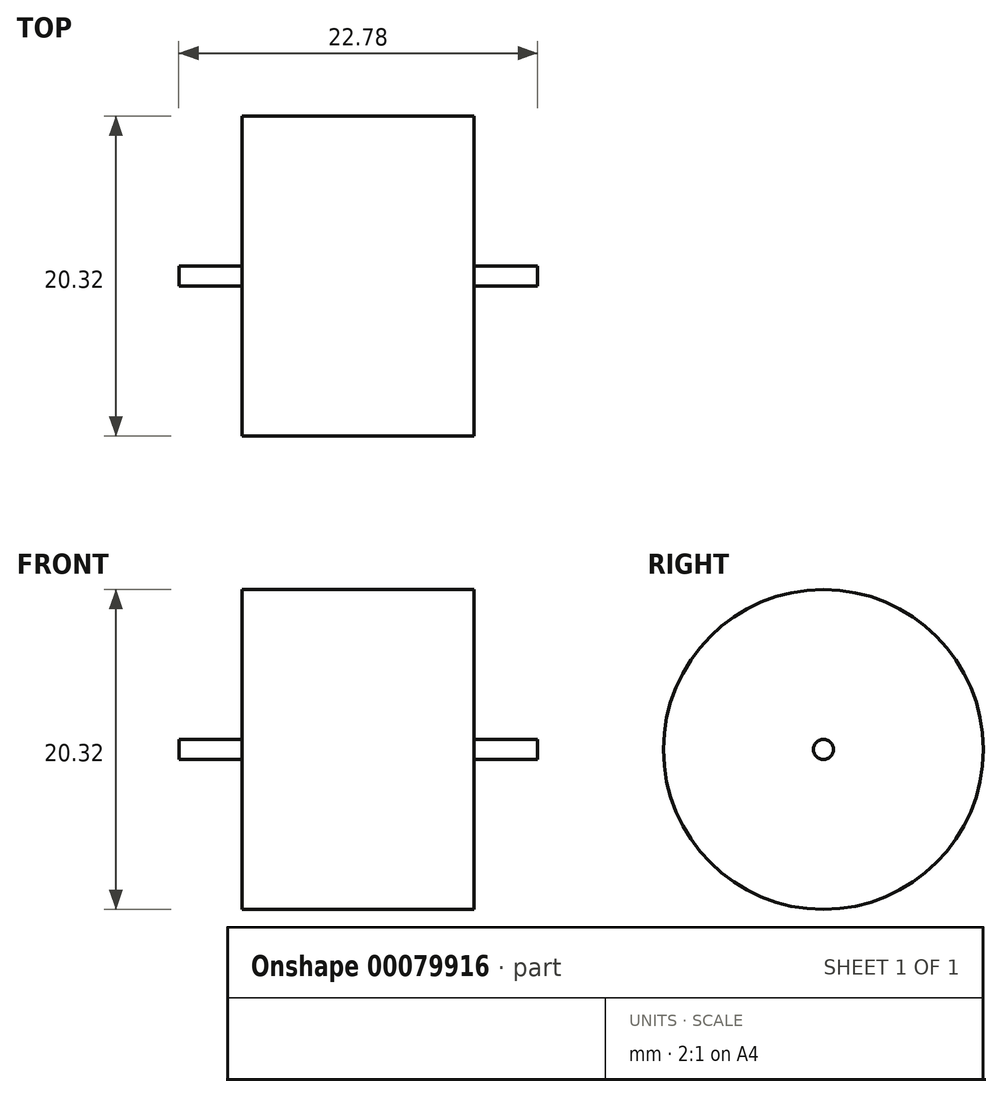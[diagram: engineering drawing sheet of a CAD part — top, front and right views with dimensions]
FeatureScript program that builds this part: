
annotation { "Feature Type Name" : "Feature", "Feature Type Description" : "" }
export const myFeature = defineFeature(function(context is Context, id is Id, definition is map)
    precondition{}
    {
        {
            var Q0;
            Q0=qCreatedBy(makeId("Right.planeOp"),FACE);
            var sketch = newSketch(context, id + "F0", { "sketchPlane" : qUnion([Q0])});
            skCircle(sketch, "E0", {"center": v(0, 0) * mm, "radius": 10.16 * mm});
            skCircle(sketch, "E1", {"center": v(0, 0) * mm, "radius": 0.64 * mm});
            skSolve(sketch);
        }
        {
            var Q0;
            Q0=makeQuery(id+"F0.imprint","IMPRINT",FACE,{"disambiguationData":[TD([[makeQuery(id+"F0.imprint","IMPRINT",EDGE,{"derivedFrom":sQuery(id+"F0.wireOp",EDGE,"E0")}),1.0]])]});
            extrude(context, id + "F1", {"entities" : qUnion([Q0]), "depth" : 7.37 * mm, "hasSecondDirection" : true, "secondDirectionOppositeDirection" : true, "secondDirectionDepth" : 7.37 * mm});
        }
        {
            var Q0;
            Q0=makeQuery(id+"F0.imprint","IMPRINT",FACE,{"disambiguationData":[TD([[makeQuery(id+"F0.imprint","IMPRINT",EDGE,{"derivedFrom":sQuery(id+"F0.wireOp",EDGE,"E1")}),1.0]])]});
            extrude(context, id + "F2", {"entities" : qUnion([Q0]), "operationType" : NewBodyOperationType.ADD, "depth" : 11.4 * mm, "hasSecondDirection" : true, "secondDirectionOppositeDirection" : true, "secondDirectionDepth" : 11.4 * mm});
        }
    });
